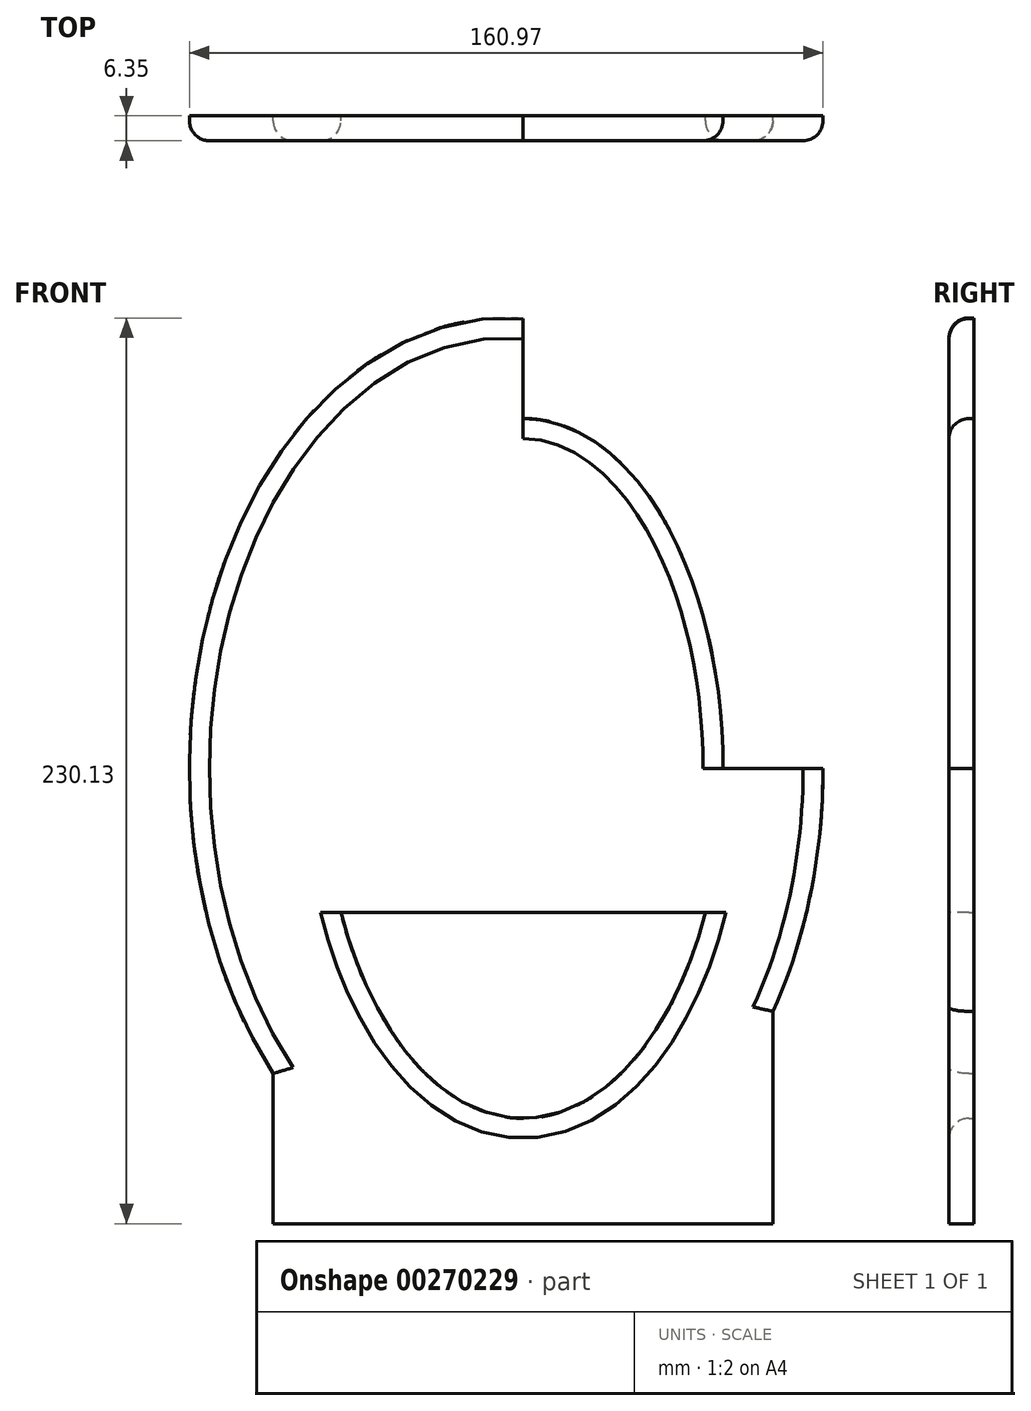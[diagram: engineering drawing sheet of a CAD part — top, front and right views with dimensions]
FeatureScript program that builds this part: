
annotation { "Feature Type Name" : "Feature", "Feature Type Description" : "" }
export const myFeature = defineFeature(function(context is Context, id is Id, definition is map)
    precondition{}
    {
        {
            var Q0;
            Q0=qCreatedBy(makeId("Front.planeOp"),FACE);
            var sketch = newSketch(context, id + "F0", { "sketchPlane" : qUnion([Q0])});
            skLineSegment(sketch, "E0", {"start": v(-4.23, 40.45) * mm, "end": v(71.97, 40.45) * mm});
            skLineSegment(sketch, "E1", {"start": v(-4.23, 40.45) * mm, "end": v(-4.23, 154.75) * mm});
            skEllipse(sketch, "E2", {"center": v(-8.51, 40.45) * mm, "majorRadius": 80.48 * mm, "minorRadius": 114.46 * mm, "majorAxis": v(1, 0)});
            skLineSegment(sketch, "E3.bottom", {"start": v(59.27, -75.2) * mm, "end": v(-67.73, -75.2) * mm});
            skLineSegment(sketch, "E3.top", {"start": v(59.27, 3.8) * mm, "end": v(-67.73, 3.8) * mm});
            skLineSegment(sketch, "E3.left", {"start": v(59.27, -75.2) * mm, "end": v(59.27, 3.8) * mm});
            skLineSegment(sketch, "E3.right", {"start": v(-67.73, -75.2) * mm, "end": v(-67.73, 3.8) * mm});
            skPoint(sketch, "E3.middle", {"position": v(-4.23, -35.7) * mm});
            skLineSegment(sketch, "E4", {"start": v(-4.23, 40.45) * mm, "end": v(-4.23, 129.35) * mm});
            skLineSegment(sketch, "E5", {"start": v(-4.23, 40.45) * mm, "end": v(46.57, 40.45) * mm});
            skEllipse(sketch, "E6", {"center": v(-4.23, 40.45) * mm, "majorRadius": 50.8 * mm, "minorRadius": 88.9 * mm, "majorAxis": v(1, 0)});
            skSolve(sketch);
        }
        {
            var Q0;
            {var subQ5=sQuery(id+"F0.wireOp",EDGE,"E3.bottom");Q0=makeQuery(id+"F0.imprint","IMPRINT",FACE,{"disambiguationData":[TD([[makeQuery(id+"F0.imprint","IMPRINT",EDGE,{"derivedFrom":subQ5}),-1.0]])]});}
            var Q1;
            {var subQ0=sQuery(id+"F0.wireOp",EDGE,"E3.left");var subQ3=sQuery(id+"F0.wireOp",EDGE,"E2");var subQ4=makeQuery(id+"F0.imprint","INTERSECT",VERTEX,{"derivedFrom":[subQ3,subQ0]});Q1=makeQuery(id+"F0.imprint","IMPRINT",FACE,{"disambiguationData":[TD([[makeQuery(id+"F0.imprint","IMPRINT",EDGE,{"disambiguationData":[TD([[subQ4,1.0]])],"derivedFrom":subQ3}),1.0]])]});}
            var Q2;
            {var subQ7=sQuery(id+"F0.wireOp",EDGE,"E1");Q2=makeQuery(id+"F0.imprint","IMPRINT",FACE,{"disambiguationData":[TD([[makeQuery(id+"F0.imprint","IMPRINT",EDGE,{"derivedFrom":subQ7}),1.0]])]});}
            var Q3;
            {var subQ0=sQuery(id+"F0.wireOp",EDGE,"E0");Q3=makeQuery(id+"F0.imprint","IMPRINT",FACE,{"disambiguationData":[TD([[makeQuery(id+"F0.imprint","IMPRINT",EDGE,{"derivedFrom":subQ0}),1.0]])]});}
            var Q4;
            {var subQ7=sQuery(id+"F0.wireOp",EDGE,"E0");Q4=makeQuery(id+"F0.imprint","IMPRINT",FACE,{"disambiguationData":[TD([[makeQuery(id+"F0.imprint","IMPRINT",EDGE,{"derivedFrom":subQ7}),-1.0]])]});}
            extrude(context, id + "F1", {"entities" : qUnion([Q0, Q1, Q2, Q3, Q4]), "depth" : 6.35 * mm});
        }
        {
            var Q0;
            Q0=makeQuery(id+"F1.opExtrude","CAP_EDGE",EDGE,{"disambiguationData":[OSD([sQuery(id+"F0.wireOp",EDGE,"E2")])],"isStart":false});
            var Q1;
            Q1=makeQuery(id+"F1.opExtrude","CAP_EDGE",EDGE,{"disambiguationData":[OSD([sQuery(id+"F0.wireOp",EDGE,"E6")])],"isStart":false});
            var Q2;
            Q2=makeQuery(id+"F1.opExtrude","CAP_EDGE",EDGE,{"disambiguationData":[OSD([sQuery(id+"F0.wireOp",EDGE,"E3.left")])],"isStart":false});
            var Q3;
            Q3=makeQuery(id+"F1.opExtrude","CAP_EDGE",EDGE,{"disambiguationData":[OSD([sQuery(id+"F0.wireOp",EDGE,"E3.right")])],"isStart":false});
            fillet(context, id + "F2", {"entities" : qUnion([Q0, Q1, Q2, Q3]), "radius" : 5.08 * mm, "tangentPropagation" : true, "allowEdgeOverflow" : false});
        }
    });
